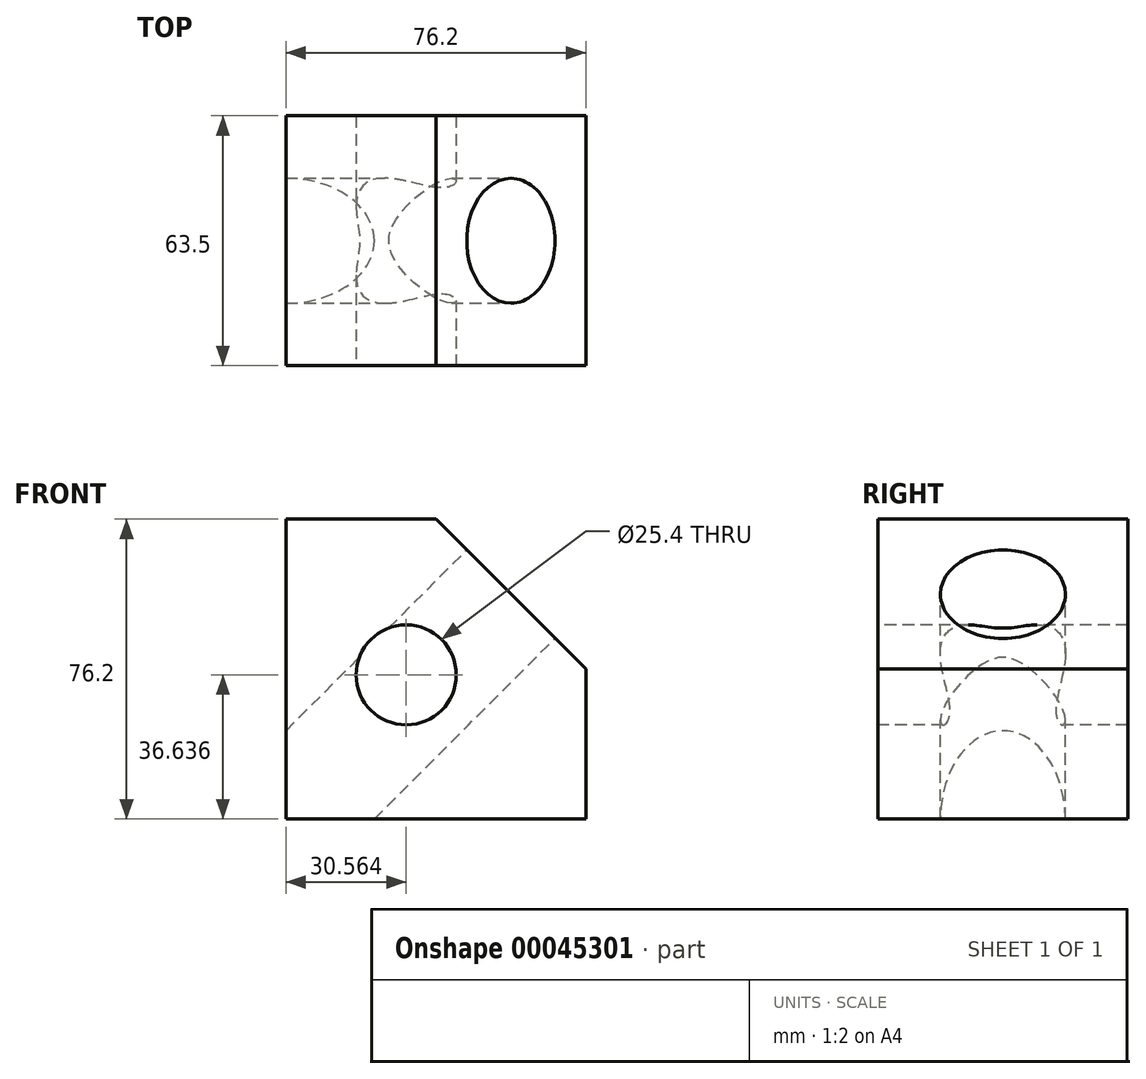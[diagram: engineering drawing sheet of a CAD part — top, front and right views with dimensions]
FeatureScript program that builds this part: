
annotation { "Feature Type Name" : "Feature", "Feature Type Description" : "" }
export const myFeature = defineFeature(function(context is Context, id is Id, definition is map)
    precondition{}
    {
        {
            var Q0;
            Q0=qCreatedBy(makeId("Front.planeOp"),FACE);
            var sketch = newSketch(context, id + "F0", { "sketchPlane" : qUnion([Q0])});
            skLineSegment(sketch, "E0", {"start": v(0, 0) * mm, "end": v(76.2, 0) * mm});
            skLineSegment(sketch, "E1", {"start": v(76.2, 0) * mm, "end": v(76.2, 38.1) * mm});
            skLineSegment(sketch, "E2", {"start": v(76.2, 38.1) * mm, "end": v(38.1, 76.2) * mm});
            skLineSegment(sketch, "E3", {"start": v(38.1, 76.2) * mm, "end": v(0, 76.2) * mm});
            skLineSegment(sketch, "E4", {"start": v(0, 76.2) * mm, "end": v(0, 0) * mm});
            skSolve(sketch);
        }
        {
            var Q0;
            Q0=makeQuery(id+"F0.imprint","IMPRINT",FACE,{"disambiguationData":[TD([[makeQuery(id+"F0.imprint","IMPRINT",EDGE,{"derivedFrom":sQuery(id+"F0.wireOp",EDGE,"E0")}),1.0]])]});
            extrude(context, id + "F1", {"entities" : qUnion([Q0]), "endBound" : BoundingType.SYMMETRIC, "depth" : 63.5 * mm});
        }
        {
            var Q0;
            Q0=makeQuery(id+"F1.opExtrude","SWEPT_FACE",FACE,{"disambiguationData":[OSD([sQuery(id+"F0.wireOp",EDGE,"E2")])]});
            var sketch = newSketch(context, id + "F2", { "sketchPlane" : qUnion([Q0])});
            skCircle(sketch, "E5", {"center": v(0, 0) * mm, "radius": 15.88 * mm});
            skSolve(sketch);
        }
        {
            var Q0;
            Q0=makeQuery(id+"F2.imprint","IMPRINT",FACE,{"disambiguationData":[TD([[makeQuery(id+"F2.imprint","IMPRINT",EDGE,{"derivedFrom":sQuery(id+"F2.wireOp",EDGE,"E5")}),1.0]])]});
            extrude(context, id + "F3", {"entities" : qUnion([Q0]), "operationType" : NewBodyOperationType.REMOVE, "endBound" : BoundingType.THROUGH_ALL, "oppositeDirection" : true, "depth" : 25.4 * mm});
        }
        {
            var Q0;
            Q0=makeQuery(id+"F1.opExtrude","CAP_FACE",FACE,{"disambiguationData":[OSD([sQuery(id+"F0.wireOp",EDGE,"E0"),sQuery(id+"F0.wireOp",EDGE,"E1"),sQuery(id+"F0.wireOp",EDGE,"E2"),sQuery(id+"F0.wireOp",EDGE,"E3"),sQuery(id+"F0.wireOp",EDGE,"E4")])],"isStart":false});
            var sketch = newSketch(context, id + "F4", { "sketchPlane" : qUnion([Q0])});
            skCircle(sketch, "E6", {"center": v(30.56, 36.64) * mm, "radius": 12.7 * mm});
            skSolve(sketch);
        }
        {
            var Q0;
            Q0=makeQuery(id+"F4.imprint","IMPRINT",FACE,{"disambiguationData":[TD([[makeQuery(id+"F4.imprint","IMPRINT",EDGE,{"derivedFrom":sQuery(id+"F4.wireOp",EDGE,"E6")}),1.0]])]});
            extrude(context, id + "F5", {"entities" : qUnion([Q0]), "operationType" : NewBodyOperationType.REMOVE, "endBound" : BoundingType.THROUGH_ALL, "oppositeDirection" : true, "depth" : 25.4 * mm});
        }
    });
